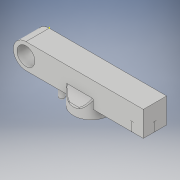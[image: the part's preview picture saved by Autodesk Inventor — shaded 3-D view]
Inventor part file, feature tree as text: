
AUTODESK INVENTOR PART (.ipt)
format: ipt  version: 2019 (Build 230136000, 136)  size: 227,328 bytes
history: native  units: in
note: dims shown in document units (in); Inventor stores cm internally (conversion verified against a paired STEP export)
features: sketch x5, extrude x4, fillet x3, chamfer x2
ambient origin geometry x8: Origin, YZ Plane, XZ Plane, XY Plane, X Axis, Y Axis, Z Axis, Center Point
bodies: Solid1 (feature_tree)
feature tree (14):
  extrude  "Extrusion1"  Depth=2.5787in
  extrude  "Extrusion2"  Depth=0.5118in TaperAngle=0.0deg
  extrude  "Extrusion3"  Depth=0.1969in TaperAngle=0.0deg
  sketch  "Sketch4"  dims[d9=2.3228in]
  chamfer  "Chamfer1"  Distance=1.1811in
  chamfer  "Chamfer2"  Distance=0.1969in
  extrude  "Extrusion4"  Depth=0.2559in
  fillet  "Fillet1"  Radius=0.2559in
  fillet  "Fillet2"  Radius=0.1181in
  fillet  "Fillet3"  Radius=0.1181in
  sketch  "Sketch1"  dims[d0=0.3937in d2=2.5787in]
  sketch  "Sketch2"  dims[d3=0.2756in d4=0.5118in d5=0.0in]
  sketch  "Sketch3"  dims[d6=0.5118in d7=0.1969in d8=0.0in]
  sketch  "Sketch5"  dims[d11=0.7874in d12=1.1811in d13=0.1969in d14=0.0in d15=0.2559in d16=0.2559in d17=0.1181in d18=0.0787in d19=120.0deg d20=0.1181in d21=0.0787in d22=120.0deg d23=0.1181in d24=0.5315in d25=0.3937in d26=0.0in d27=0.0394in d28=0.0394in d29=0.0394in]
